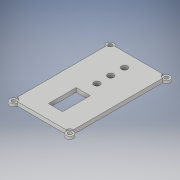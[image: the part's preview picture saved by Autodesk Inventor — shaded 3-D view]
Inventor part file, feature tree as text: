
AUTODESK INVENTOR PART (.ipt)
format: ipt  version: 2019 (Build 230136000, 136)  size: 189,952 bytes
history: native  units: mm
features: extrude x5, sketch x5, projected_geometry x2
ambient origin geometry x8: Origin, YZ Plane, XZ Plane, XY Plane, X Axis, Y Axis, Z Axis, Center Point
bodies: Solid1 (feature_tree)
feature tree (12):
  extrude  "Extrusion1"  Depth=110.0mm
  extrude  "Extrusion2"  Depth=110.0mm
  extrude  "Extrusion3"  Depth=3.0mm
  extrude  "Extrusion4"  Depth=3.0mm TaperAngle=0.0deg
  extrude  "Extrusion5"  Depth=31.5mm
  sketch  "Sketch1"  dims[d0=64.0mm d1=110.0mm]
  sketch  "Sketch2"  dims[d2=8.485mm d3=20.0mm d5=110.0mm d6=20.0mm d8=64.0mm]
  projected_geometry  "Projected Loop1"
  sketch  "Sketch3"  dims[d11=3.0mm d12=0.0mm d13=4.3mm]
  sketch  "Sketch4"  dims[d14=20.0mm d16=110.0mm d17=20.0mm d19=64.0mm d22=3.0mm d23=0.0mm]
  sketch  "Sketch5"  dims[d24=16.0mm d25=31.5mm d26=24.0mm d27=24.0mm d28=15.7mm d29=3.0mm d30=0.0mm d31=6.8mm d32=6.8mm d33=6.8mm d34=15.7mm d35=15.7mm d36=15.7mm d37=15.7mm d38=3.0mm d39=0.0mm d40=20.0mm d42=110.0mm d43=20.0mm d45=64.0mm d48=1.5mm d49=0.0mm]
  projected_geometry  "Projected Loop2"
